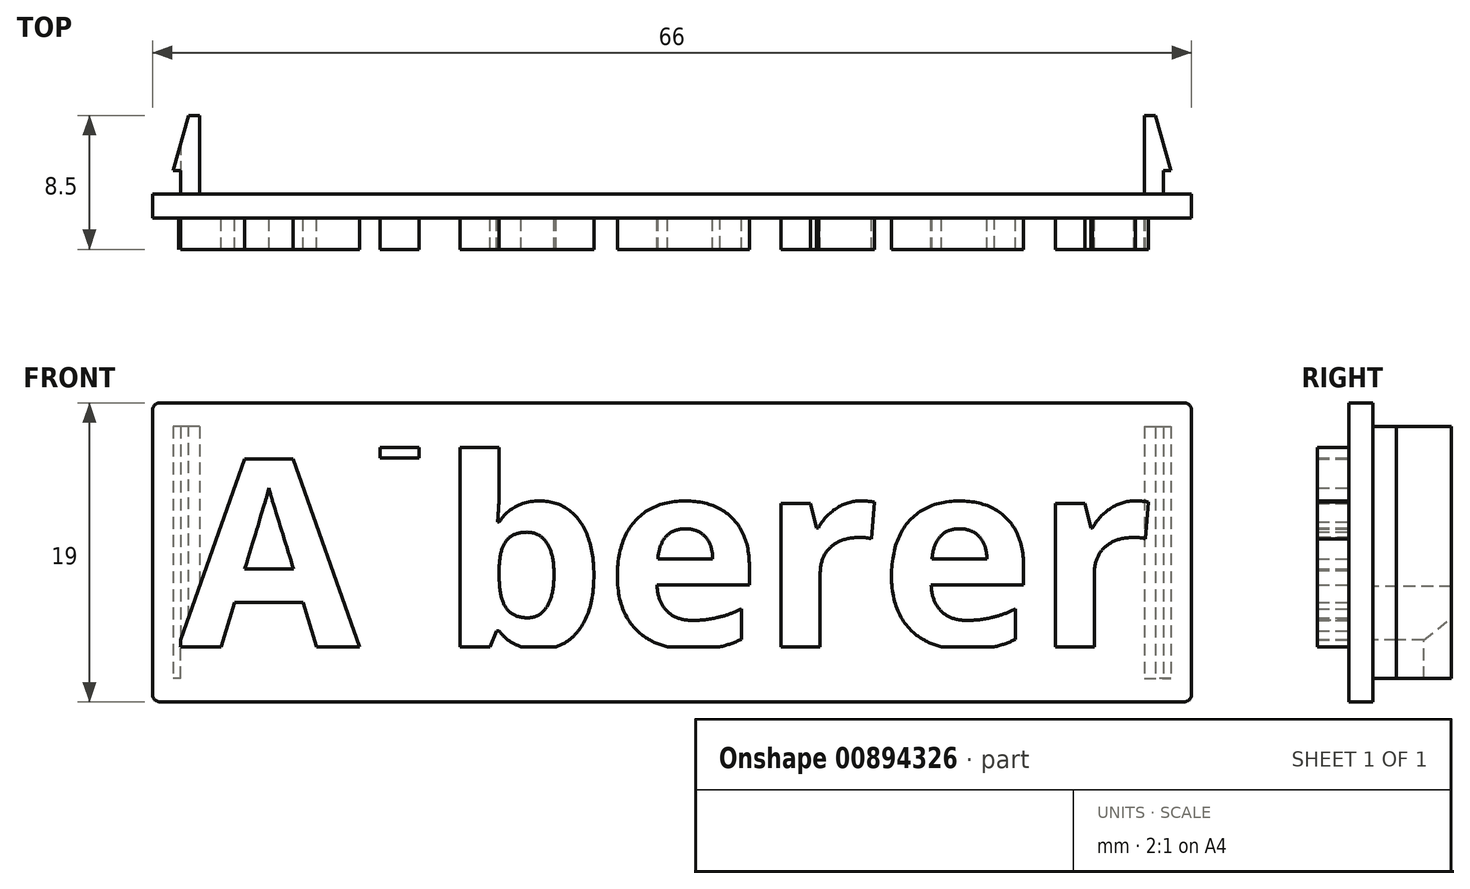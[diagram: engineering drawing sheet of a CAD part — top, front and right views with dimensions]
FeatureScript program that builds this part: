
annotation { "Feature Type Name" : "Feature", "Feature Type Description" : "" }
export const myFeature = defineFeature(function(context is Context, id is Id, definition is map)
    precondition{}
    {
        {
            var Q0;
            Q0=qCreatedBy(makeId("Front.planeOp"),FACE);
            var sketch = newSketch(context, id + "F0", { "sketchPlane" : qUnion([Q0])});
            skLineSegment(sketch, "E0.bottom", {"start": v(33, -9.5) * mm, "end": v(-33, -9.5) * mm});
            skLineSegment(sketch, "E0.top", {"start": v(33, 9.5) * mm, "end": v(-33, 9.5) * mm});
            skLineSegment(sketch, "E0.left", {"start": v(33, -9.5) * mm, "end": v(33, 9.5) * mm});
            skLineSegment(sketch, "E0.right", {"start": v(-33, -9.5) * mm, "end": v(-33, 9.5) * mm});
            skPoint(sketch, "E0.middle", {"position": v(0, 0) * mm});
            skLineSegment(sketch, "E1.bottom", {"start": v(31.35, -6) * mm, "end": v(-31.35, -6) * mm});
            skLineSegment(sketch, "E1.top", {"start": v(31.35, 6) * mm, "end": v(-31.35, 6) * mm});
            skLineSegment(sketch, "E1.left", {"start": v(31.35, -6) * mm, "end": v(31.35, 6) * mm});
            skLineSegment(sketch, "E1.right", {"start": v(-31.35, -6) * mm, "end": v(-31.35, 6) * mm});
            skText(sketch, "E2", { "text": "Alberer", "fontName": "OpenSans-Bold.ttf"});
            skLineSegment(sketch, "E3", {"start": v(31.2, 9.5) * mm, "end": v(31.2, -9.5) * mm});
            skLineSegment(sketch, "E4", {"start": v(30, 9.5) * mm, "end": v(30, -9.5) * mm});
            skLineSegment(sketch, "E5", {"start": v(31.7, 9.5) * mm, "end": v(31.7, -9.5) * mm});
            skLineSegment(sketch, "E6.MirrorCS", {"start": v(-30, 9.5) * mm, "end": v(-30, -9.5) * mm});
            skLineSegment(sketch, "E7.MirrorCS", {"start": v(-31.2, 9.5) * mm, "end": v(-31.2, -9.5) * mm});
            skLineSegment(sketch, "E8.MirrorCS", {"start": v(-31.7, 9.5) * mm, "end": v(-31.7, -9.5) * mm});
            skLineSegment(sketch, "E9", {"start": v(-30, 8) * mm, "end": v(-31.7, 8) * mm});
            skLineSegment(sketch, "E10.MirrorCS", {"start": v(-30, -8) * mm, "end": v(-31.7, -8) * mm});
            skLineSegment(sketch, "E11.MirrorCS", {"start": v(30, 8) * mm, "end": v(31.7, 8) * mm});
            skLineSegment(sketch, "E12.MirrorCS", {"start": v(30, -8) * mm, "end": v(31.7, -8) * mm});
            const initialGuessF0  = {"E2": [-0.03135, -0.006, 1, 0, 0.012]};
            skSetInitialGuess(sketch, initialGuessF0);
            skSolve(sketch);
        }
        {
            var Q0;
            Q0 = qSketchRegion(id + "F0", true);
            var Q1;
            {var subQ0=sQuery(id+"F0.wireOp",EDGE,"E2.sketch_text.stroke-93");Q1=makeQuery(id+"F0.imprint","IMPRINT",FACE,{"disambiguationData":[TD([[makeQuery(id+"F0.imprint","IMPRINT",EDGE,{"derivedFrom":subQ0}),-1.0]])]});}
            var Q2;
            Q2=makeQuery(id+"F0.imprint","IMPRINT",FACE,{"disambiguationData":[TD([[makeQuery(id+"F0.imprint","IMPRINT",EDGE,{"derivedFrom":sQuery(id+"F0.wireOp",EDGE,"E2.sketch_text.stroke-16")}),-1.0]])]});
            var Q3;
            {var subQ0=sQuery(id+"F0.wireOp",EDGE,"E6.MirrorCS");var subQ1=sQuery(id+"F0.wireOp",EDGE,"E0.bottom");var subQ2=makeQuery(id+"F0.imprint","INTERSECT",VERTEX,{"derivedFrom":[subQ1,subQ0]});Q3=makeQuery(id+"F0.imprint","IMPRINT",FACE,{"disambiguationData":[TD([[makeQuery(id+"F0.imprint","IMPRINT",EDGE,{"disambiguationData":[TD([[subQ2,-1.0]])],"derivedFrom":subQ1}),-1.0]])]});}
            var Q4;
            {var subQ3=sQuery(id+"F0.wireOp",EDGE,"E3");var subQ5=sQuery(id+"F0.wireOp",EDGE,"E2.sketch_text.stroke-95");var subQ6=makeQuery(id+"F0.imprint","INTERSECT",VERTEX,{"derivedFrom":[subQ5,subQ3]});Q4=makeQuery(id+"F0.imprint","IMPRINT",FACE,{"disambiguationData":[TD([[makeQuery(id+"F0.imprint","IMPRINT",EDGE,{"disambiguationData":[TD([[subQ6,-1.0]])],"derivedFrom":subQ5}),-1.0]])]});}
            var Q5;
            Q5=makeQuery(id+"F0.imprint","IMPRINT",FACE,{"disambiguationData":[TD([[makeQuery(id+"F0.imprint","IMPRINT",EDGE,{"derivedFrom":sQuery(id+"F0.wireOp",EDGE,"E2.sketch_text.stroke-0")}),-1.0]])]});
            var Q6;
            Q6=makeQuery(id+"F0.imprint","IMPRINT",FACE,{"disambiguationData":[TD([[makeQuery(id+"F0.imprint","IMPRINT",EDGE,{"derivedFrom":sQuery(id+"F0.wireOp",EDGE,"E2.sketch_text.stroke-39")}),-1.0]])]});
            var Q7;
            {var subQ6=sQuery(id+"F0.wireOp",EDGE,"E0.right");Q7=makeQuery(id+"F0.imprint","IMPRINT",FACE,{"disambiguationData":[TD([[makeQuery(id+"F0.imprint","IMPRINT",EDGE,{"derivedFrom":subQ6}),-1.0]])]});}
            var Q8;
            {var subQ0=sQuery(id+"F0.wireOp",EDGE,"E6.MirrorCS");var subQ1=sQuery(id+"F0.wireOp",EDGE,"E1.top");var subQ2=makeQuery(id+"F0.imprint","INTERSECT",VERTEX,{"derivedFrom":[subQ1,subQ0]});Q8=makeQuery(id+"F0.imprint","IMPRINT",FACE,{"disambiguationData":[TD([[makeQuery(id+"F0.imprint","IMPRINT",EDGE,{"disambiguationData":[TD([[subQ2,-1.0]])],"derivedFrom":subQ1}),1.0]])]});}
            var Q9;
            Q9=makeQuery(id+"F0.imprint","IMPRINT",FACE,{"disambiguationData":[TD([[makeQuery(id+"F0.imprint","IMPRINT",EDGE,{"derivedFrom":sQuery(id+"F0.wireOp",EDGE,"E2.sketch_text.stroke-59")}),-1.0]])]});
            var Q10;
            {var subQ0=sQuery(id+"F0.wireOp",EDGE,"E1.right");Q10=makeQuery(id+"F0.imprint","IMPRINT",FACE,{"disambiguationData":[TD([[makeQuery(id+"F0.imprint","IMPRINT",EDGE,{"derivedFrom":subQ0}),-1.0]])]});}
            var Q11;
            {var subQ4=sQuery(id+"F0.wireOp",EDGE,"E1.left");Q11=makeQuery(id+"F0.imprint","IMPRINT",FACE,{"disambiguationData":[TD([[makeQuery(id+"F0.imprint","IMPRINT",EDGE,{"derivedFrom":subQ4}),1.0]])]});}
            var Q12;
            {var subQ3=sQuery(id+"F0.wireOp",EDGE,"E2.sketch_text.stroke-24");var subQ5=sQuery(id+"F0.wireOp",EDGE,"E1.top");var subQ7=makeQuery(id+"F0.imprint","INTERSECT",VERTEX,{"derivedFrom":[subQ5,subQ3]});Q12=makeQuery(id+"F0.imprint","IMPRINT",FACE,{"disambiguationData":[TD([[makeQuery(id+"F0.imprint","IMPRINT",EDGE,{"disambiguationData":[TD([[subQ7,-1.0]])],"derivedFrom":subQ5}),1.0]])]});}
            var Q13;
            Q13=makeQuery(id+"F0.imprint","IMPRINT",FACE,{"disambiguationData":[TD([[makeQuery(id+"F0.imprint","IMPRINT",EDGE,{"derivedFrom":sQuery(id+"F0.wireOp",EDGE,"E2.sketch_text.stroke-30")}),1.0]])]});
            var Q14;
            {var subQ4=sQuery(id+"F0.wireOp",EDGE,"E2.sketch_text.stroke-96");Q14=makeQuery(id+"F0.imprint","IMPRINT",FACE,{"disambiguationData":[TD([[makeQuery(id+"F0.imprint","IMPRINT",EDGE,{"derivedFrom":subQ4}),1.0]])]});}
            var Q15;
            {var subQ4=sQuery(id+"F0.wireOp",EDGE,"E0.left");Q15=makeQuery(id+"F0.imprint","IMPRINT",FACE,{"disambiguationData":[TD([[makeQuery(id+"F0.imprint","IMPRINT",EDGE,{"derivedFrom":subQ4}),1.0]])]});}
            var Q16;
            {var subQ0=sQuery(id+"F0.wireOp",EDGE,"E6.MirrorCS");var subQ1=sQuery(id+"F0.wireOp",EDGE,"E0.top");var subQ2=makeQuery(id+"F0.imprint","INTERSECT",VERTEX,{"derivedFrom":[subQ1,subQ0]});Q16=makeQuery(id+"F0.imprint","IMPRINT",FACE,{"disambiguationData":[TD([[makeQuery(id+"F0.imprint","IMPRINT",EDGE,{"disambiguationData":[TD([[subQ2,-1.0]])],"derivedFrom":subQ1}),1.0]])]});}
            var Q17;
            {var subQ6=sQuery(id+"F0.wireOp",EDGE,"E2.sketch_text.stroke-0");Q17=makeQuery(id+"F0.imprint","IMPRINT",FACE,{"disambiguationData":[TD([[makeQuery(id+"F0.imprint","IMPRINT",EDGE,{"derivedFrom":subQ6}),1.0]])]});}
            var Q18;
            {var subQ3=sQuery(id+"F0.wireOp",EDGE,"E2.sketch_text.stroke-4");var subQ5=sQuery(id+"F0.wireOp",EDGE,"E7.MirrorCS");var subQ6=makeQuery(id+"F0.imprint","INTERSECT",VERTEX,{"derivedFrom":[subQ3,subQ5]});Q18=makeQuery(id+"F0.imprint","IMPRINT",FACE,{"disambiguationData":[TD([[makeQuery(id+"F0.imprint","IMPRINT",EDGE,{"disambiguationData":[TD([[subQ6,-1.0]])],"derivedFrom":subQ3}),-1.0]])]});}
            var Q19;
            {var subQ1=sQuery(id+"F0.wireOp",EDGE,"E2.sketch_text.stroke-3");var subQ3=sQuery(id+"F0.wireOp",EDGE,"E8.MirrorCS");var subQ4=makeQuery(id+"F0.imprint","INTERSECT",VERTEX,{"derivedFrom":[subQ1,subQ3]});Q19=makeQuery(id+"F0.imprint","IMPRINT",FACE,{"disambiguationData":[TD([[makeQuery(id+"F0.imprint","IMPRINT",EDGE,{"disambiguationData":[TD([[subQ4,1.0]])],"derivedFrom":subQ3}),-1.0]])]});}
            var Q20;
            {var subQ0=sQuery(id+"F0.wireOp",EDGE,"E3");var subQ1=sQuery(id+"F0.wireOp",EDGE,"E1.top");var subQ2=makeQuery(id+"F0.imprint","INTERSECT",VERTEX,{"derivedFrom":[subQ1,subQ0]});Q20=makeQuery(id+"F0.imprint","IMPRINT",FACE,{"disambiguationData":[TD([[makeQuery(id+"F0.imprint","IMPRINT",EDGE,{"disambiguationData":[TD([[subQ2,-1.0]])],"derivedFrom":subQ1}),1.0]])]});}
            var Q21;
            {var subQ1=sQuery(id+"F0.wireOp",EDGE,"E2.sketch_text.stroke-7");Q21=makeQuery(id+"F0.imprint","IMPRINT",FACE,{"disambiguationData":[TD([[makeQuery(id+"F0.imprint","IMPRINT",EDGE,{"derivedFrom":subQ1}),1.0]])]});}
            var Q22;
            Q22=makeQuery(id+"F0.imprint","IMPRINT",FACE,{"disambiguationData":[TD([[makeQuery(id+"F0.imprint","IMPRINT",EDGE,{"derivedFrom":sQuery(id+"F0.wireOp",EDGE,"E2.sketch_text.stroke-72")}),1.0]])]});
            var Q23;
            {var subQ0=sQuery(id+"F0.wireOp",EDGE,"E3");var subQ1=sQuery(id+"F0.wireOp",EDGE,"E0.top");var subQ2=makeQuery(id+"F0.imprint","INTERSECT",VERTEX,{"derivedFrom":[subQ1,subQ0]});Q23=makeQuery(id+"F0.imprint","IMPRINT",FACE,{"disambiguationData":[TD([[makeQuery(id+"F0.imprint","IMPRINT",EDGE,{"disambiguationData":[TD([[subQ2,-1.0]])],"derivedFrom":subQ1}),1.0]])]});}
            var Q24;
            {var subQ0=sQuery(id+"F0.wireOp",EDGE,"E3");var subQ1=sQuery(id+"F0.wireOp",EDGE,"E1.bottom");var subQ2=makeQuery(id+"F0.imprint","INTERSECT",VERTEX,{"derivedFrom":[subQ1,subQ0]});Q24=makeQuery(id+"F0.imprint","IMPRINT",FACE,{"disambiguationData":[TD([[makeQuery(id+"F0.imprint","IMPRINT",EDGE,{"disambiguationData":[TD([[subQ2,-1.0]])],"derivedFrom":subQ1}),-1.0]])]});}
            var Q25;
            {var subQ0=sQuery(id+"F0.wireOp",EDGE,"E3");var subQ1=sQuery(id+"F0.wireOp",EDGE,"E0.bottom");var subQ2=makeQuery(id+"F0.imprint","INTERSECT",VERTEX,{"derivedFrom":[subQ1,subQ0]});Q25=makeQuery(id+"F0.imprint","IMPRINT",FACE,{"disambiguationData":[TD([[makeQuery(id+"F0.imprint","IMPRINT",EDGE,{"disambiguationData":[TD([[subQ2,-1.0]])],"derivedFrom":subQ1}),-1.0]])]});}
            var Q26;
            {var subQ5=sQuery(id+"F0.wireOp",EDGE,"E2.sketch_text.stroke-12");Q26=makeQuery(id+"F0.imprint","IMPRINT",FACE,{"disambiguationData":[TD([[makeQuery(id+"F0.imprint","IMPRINT",EDGE,{"derivedFrom":subQ5}),-1.0]])]});}
            var Q27;
            {var subQ7=sQuery(id+"F0.wireOp",EDGE,"E2.sketch_text.stroke-14");Q27=makeQuery(id+"F0.imprint","IMPRINT",FACE,{"disambiguationData":[TD([[makeQuery(id+"F0.imprint","IMPRINT",EDGE,{"derivedFrom":subQ7}),1.0]])]});}
            var Q28;
            {var subQ0=sQuery(id+"F0.wireOp",EDGE,"E2.sketch_text.stroke-5");Q28=makeQuery(id+"F0.imprint","IMPRINT",FACE,{"disambiguationData":[TD([[makeQuery(id+"F0.imprint","IMPRINT",EDGE,{"derivedFrom":subQ0}),1.0]])]});}
            var Q29;
            Q29=makeQuery(id+"F0.imprint","IMPRINT",FACE,{"disambiguationData":[TD([[makeQuery(id+"F0.imprint","IMPRINT",EDGE,{"derivedFrom":sQuery(id+"F0.wireOp",EDGE,"E2.sketch_text.stroke-16")}),1.0]])]});
            var Q30;
            Q30=makeQuery(id+"F0.imprint","IMPRINT",FACE,{"disambiguationData":[TD([[makeQuery(id+"F0.imprint","IMPRINT",EDGE,{"derivedFrom":sQuery(id+"F0.wireOp",EDGE,"E2.sketch_text.stroke-8")}),1.0]])]});
            var Q31;
            {var subQ0=sQuery(id+"F0.wireOp",EDGE,"E2.sketch_text.stroke-96");Q31=makeQuery(id+"F0.imprint","IMPRINT",FACE,{"disambiguationData":[TD([[makeQuery(id+"F0.imprint","IMPRINT",EDGE,{"derivedFrom":subQ0}),-1.0]])]});}
            var Q32;
            {var subQ1=sQuery(id+"F0.wireOp",EDGE,"E1.bottom");var subQ3=sQuery(id+"F0.wireOp",EDGE,"E6.MirrorCS");var subQ4=makeQuery(id+"F0.imprint","INTERSECT",VERTEX,{"derivedFrom":[subQ1,subQ3]});Q32=makeQuery(id+"F0.imprint","IMPRINT",FACE,{"disambiguationData":[TD([[makeQuery(id+"F0.imprint","IMPRINT",EDGE,{"disambiguationData":[TD([[subQ4,1.0]])],"derivedFrom":subQ3}),-1.0]])]});}
            var Q33;
            Q33=makeQuery(id+"F0.imprint","IMPRINT",FACE,{"disambiguationData":[TD([[makeQuery(id+"F0.imprint","IMPRINT",EDGE,{"derivedFrom":sQuery(id+"F0.wireOp",EDGE,"E2.sketch_text.stroke-72")}),-1.0]])]});
            var Q34;
            {var subQ4=sQuery(id+"F0.wireOp",EDGE,"E2.sketch_text.stroke-21");Q34=makeQuery(id+"F0.imprint","IMPRINT",FACE,{"disambiguationData":[TD([[makeQuery(id+"F0.imprint","IMPRINT",EDGE,{"derivedFrom":subQ4}),1.0]])]});}
            var Q35;
            Q35=makeQuery(id+"F0.imprint","IMPRINT",FACE,{"disambiguationData":[TD([[makeQuery(id+"F0.imprint","IMPRINT",EDGE,{"derivedFrom":sQuery(id+"F0.wireOp",EDGE,"E2.sketch_text.stroke-39")}),1.0]])]});
            var Q36;
            {var subQ0=sQuery(id+"F0.wireOp",EDGE,"E7.MirrorCS");var subQ1=sQuery(id+"F0.wireOp",EDGE,"E0.top");var subQ2=makeQuery(id+"F0.imprint","INTERSECT",VERTEX,{"derivedFrom":[subQ1,subQ0]});Q36=makeQuery(id+"F0.imprint","IMPRINT",FACE,{"disambiguationData":[TD([[makeQuery(id+"F0.imprint","IMPRINT",EDGE,{"disambiguationData":[TD([[subQ2,-1.0]])],"derivedFrom":subQ1}),1.0]])]});}
            var Q37;
            {var subQ0=sQuery(id+"F0.wireOp",EDGE,"E2.sketch_text.stroke-104");var subQ1=sQuery(id+"F0.wireOp",EDGE,"E2.sketch_text.stroke-92");var subQ2=makeQuery(id+"F0.imprint","INTERSECT",VERTEX,{"derivedFrom":[subQ1,subQ0]});Q37=makeQuery(id+"F0.imprint","IMPRINT",FACE,{"disambiguationData":[TD([[makeQuery(id+"F0.imprint","IMPRINT",EDGE,{"disambiguationData":[TD([[subQ2,-1.0]])],"derivedFrom":subQ1}),-1.0]])]});}
            var Q38;
            {var subQ5=sQuery(id+"F0.wireOp",EDGE,"E1.top");var subQ7=sQuery(id+"F0.wireOp",EDGE,"E5");var subQ9=makeQuery(id+"F0.imprint","INTERSECT",VERTEX,{"derivedFrom":[subQ5,subQ7]});Q38=makeQuery(id+"F0.imprint","IMPRINT",FACE,{"disambiguationData":[TD([[makeQuery(id+"F0.imprint","IMPRINT",EDGE,{"disambiguationData":[TD([[subQ9,-1.0]])],"derivedFrom":subQ5}),1.0]])]});}
            var Q39;
            {var subQ0=sQuery(id+"F0.wireOp",EDGE,"E7.MirrorCS");var subQ1=sQuery(id+"F0.wireOp",EDGE,"E1.top");var subQ2=makeQuery(id+"F0.imprint","INTERSECT",VERTEX,{"derivedFrom":[subQ1,subQ0]});Q39=makeQuery(id+"F0.imprint","IMPRINT",FACE,{"disambiguationData":[TD([[makeQuery(id+"F0.imprint","IMPRINT",EDGE,{"disambiguationData":[TD([[subQ2,-1.0]])],"derivedFrom":subQ1}),1.0]])]});}
            var Q40;
            {var subQ5=sQuery(id+"F0.wireOp",EDGE,"E2.sketch_text.stroke-14");Q40=makeQuery(id+"F0.imprint","IMPRINT",FACE,{"disambiguationData":[TD([[makeQuery(id+"F0.imprint","IMPRINT",EDGE,{"derivedFrom":subQ5}),-1.0]])]});}
            var Q41;
            {var subQ1=sQuery(id+"F0.wireOp",EDGE,"E1.bottom");var subQ7=sQuery(id+"F0.wireOp",EDGE,"E5");var subQ9=makeQuery(id+"F0.imprint","INTERSECT",VERTEX,{"derivedFrom":[subQ1,subQ7]});Q41=makeQuery(id+"F0.imprint","IMPRINT",FACE,{"disambiguationData":[TD([[makeQuery(id+"F0.imprint","IMPRINT",EDGE,{"disambiguationData":[TD([[subQ9,-1.0]])],"derivedFrom":subQ1}),-1.0]])]});}
            var Q42;
            {var subQ0=sQuery(id+"F0.wireOp",EDGE,"E3");var subQ1=sQuery(id+"F0.wireOp",EDGE,"E0.bottom");var subQ2=makeQuery(id+"F0.imprint","INTERSECT",VERTEX,{"derivedFrom":[subQ1,subQ0]});Q42=makeQuery(id+"F0.imprint","IMPRINT",FACE,{"disambiguationData":[TD([[makeQuery(id+"F0.imprint","IMPRINT",EDGE,{"disambiguationData":[TD([[subQ2,1.0]])],"derivedFrom":subQ1}),-1.0]])]});}
            var Q43;
            {var subQ0=sQuery(id+"F0.wireOp",EDGE,"E7.MirrorCS");var subQ1=sQuery(id+"F0.wireOp",EDGE,"E0.bottom");var subQ2=makeQuery(id+"F0.imprint","INTERSECT",VERTEX,{"derivedFrom":[subQ1,subQ0]});Q43=makeQuery(id+"F0.imprint","IMPRINT",FACE,{"disambiguationData":[TD([[makeQuery(id+"F0.imprint","IMPRINT",EDGE,{"disambiguationData":[TD([[subQ2,-1.0]])],"derivedFrom":subQ1}),-1.0]])]});}
            var Q44;
            {var subQ5=sQuery(id+"F0.wireOp",EDGE,"E2.sketch_text.stroke-25");Q44=makeQuery(id+"F0.imprint","IMPRINT",FACE,{"disambiguationData":[TD([[makeQuery(id+"F0.imprint","IMPRINT",EDGE,{"derivedFrom":subQ5}),-1.0]])]});}
            var Q45;
            {var subQ0=sQuery(id+"F0.wireOp",EDGE,"E7.MirrorCS");var subQ1=sQuery(id+"F0.wireOp",EDGE,"E2.sketch_text.stroke-3");var subQ2=makeQuery(id+"F0.imprint","INTERSECT",VERTEX,{"derivedFrom":[subQ1,subQ0]});Q45=makeQuery(id+"F0.imprint","IMPRINT",FACE,{"disambiguationData":[TD([[makeQuery(id+"F0.imprint","IMPRINT",EDGE,{"disambiguationData":[TD([[subQ2,-1.0]])],"derivedFrom":subQ1}),-1.0]])]});}
            var Q46;
            {var subQ0=sQuery(id+"F0.wireOp",EDGE,"E3");var subQ1=sQuery(id+"F0.wireOp",EDGE,"E0.top");var subQ2=makeQuery(id+"F0.imprint","INTERSECT",VERTEX,{"derivedFrom":[subQ1,subQ0]});Q46=makeQuery(id+"F0.imprint","IMPRINT",FACE,{"disambiguationData":[TD([[makeQuery(id+"F0.imprint","IMPRINT",EDGE,{"disambiguationData":[TD([[subQ2,1.0]])],"derivedFrom":subQ1}),1.0]])]});}
            var Q47;
            {var subQ5=sQuery(id+"F0.wireOp",EDGE,"E2.sketch_text.stroke-91");Q47=makeQuery(id+"F0.imprint","IMPRINT",FACE,{"disambiguationData":[TD([[makeQuery(id+"F0.imprint","IMPRINT",EDGE,{"derivedFrom":subQ5}),-1.0]])]});}
            var Q48;
            {var subQ0=sQuery(id+"F0.wireOp",EDGE,"E2.sketch_text.stroke-19");var subQ1=sQuery(id+"F0.wireOp",EDGE,"E1.bottom");var subQ2=makeQuery(id+"F0.imprint","INTERSECT",VERTEX,{"derivedFrom":[subQ1,subQ0]});Q48=makeQuery(id+"F0.imprint","IMPRINT",FACE,{"disambiguationData":[TD([[makeQuery(id+"F0.imprint","IMPRINT",EDGE,{"disambiguationData":[TD([[subQ2,-1.0]])],"derivedFrom":subQ1}),1.0]])]});}
            var Q49;
            {var subQ5=sQuery(id+"F0.wireOp",EDGE,"E2.sketch_text.stroke-58");Q49=makeQuery(id+"F0.imprint","IMPRINT",FACE,{"disambiguationData":[TD([[makeQuery(id+"F0.imprint","IMPRINT",EDGE,{"derivedFrom":subQ5}),-1.0]])]});}
            var Q50;
            {var subQ0=sQuery(id+"F0.wireOp",EDGE,"E6.MirrorCS");var subQ1=sQuery(id+"F0.wireOp",EDGE,"E1.top");var subQ2=makeQuery(id+"F0.imprint","INTERSECT",VERTEX,{"derivedFrom":[subQ1,subQ0]});Q50=makeQuery(id+"F0.imprint","IMPRINT",FACE,{"disambiguationData":[TD([[makeQuery(id+"F0.imprint","IMPRINT",EDGE,{"disambiguationData":[TD([[subQ2,-1.0]])],"derivedFrom":subQ1}),-1.0]])]});}
            var Q51;
            {var subQ0=sQuery(id+"F0.wireOp",EDGE,"E7.MirrorCS");var subQ1=sQuery(id+"F0.wireOp",EDGE,"E1.top");var subQ2=makeQuery(id+"F0.imprint","INTERSECT",VERTEX,{"derivedFrom":[subQ1,subQ0]});Q51=makeQuery(id+"F0.imprint","IMPRINT",FACE,{"disambiguationData":[TD([[makeQuery(id+"F0.imprint","IMPRINT",EDGE,{"disambiguationData":[TD([[subQ2,-1.0]])],"derivedFrom":subQ1}),-1.0]])]});}
            var Q52;
            {var subQ0=sQuery(id+"F0.wireOp",EDGE,"E7.MirrorCS");var subQ1=sQuery(id+"F0.wireOp",EDGE,"E2.sketch_text.stroke-3");var subQ2=makeQuery(id+"F0.imprint","INTERSECT",VERTEX,{"derivedFrom":[subQ1,subQ0]});Q52=makeQuery(id+"F0.imprint","IMPRINT",FACE,{"disambiguationData":[TD([[makeQuery(id+"F0.imprint","IMPRINT",EDGE,{"disambiguationData":[TD([[subQ2,-1.0]])],"derivedFrom":subQ1}),1.0]])]});}
            var Q53;
            {var subQ0=sQuery(id+"F0.wireOp",EDGE,"E10.MirrorCS");var subQ1=sQuery(id+"F0.wireOp",EDGE,"E6.MirrorCS");var subQ2=makeQuery(id+"F0.imprint","INTERSECT",VERTEX,{"derivedFrom":[subQ1,subQ0]});Q53=makeQuery(id+"F0.imprint","IMPRINT",FACE,{"disambiguationData":[TD([[makeQuery(id+"F0.imprint","IMPRINT",EDGE,{"disambiguationData":[TD([[subQ2,1.0]])],"derivedFrom":subQ1}),-1.0]])]});}
            var Q54;
            {var subQ0=sQuery(id+"F0.wireOp",EDGE,"E5");var subQ1=sQuery(id+"F0.wireOp",EDGE,"E1.top");var subQ2=makeQuery(id+"F0.imprint","INTERSECT",VERTEX,{"derivedFrom":[subQ1,subQ0]});Q54=makeQuery(id+"F0.imprint","IMPRINT",FACE,{"disambiguationData":[TD([[makeQuery(id+"F0.imprint","IMPRINT",EDGE,{"disambiguationData":[TD([[subQ2,-1.0]])],"derivedFrom":subQ1}),-1.0]])]});}
            var Q55;
            {var subQ0=sQuery(id+"F0.wireOp",EDGE,"E3");var subQ1=sQuery(id+"F0.wireOp",EDGE,"E1.top");var subQ2=makeQuery(id+"F0.imprint","INTERSECT",VERTEX,{"derivedFrom":[subQ1,subQ0]});Q55=makeQuery(id+"F0.imprint","IMPRINT",FACE,{"disambiguationData":[TD([[makeQuery(id+"F0.imprint","IMPRINT",EDGE,{"disambiguationData":[TD([[subQ2,-1.0]])],"derivedFrom":subQ1}),-1.0]])]});}
            var Q56;
            {var subQ0=sQuery(id+"F0.wireOp",EDGE,"E5");var subQ1=sQuery(id+"F0.wireOp",EDGE,"E1.bottom");var subQ2=makeQuery(id+"F0.imprint","INTERSECT",VERTEX,{"derivedFrom":[subQ1,subQ0]});Q56=makeQuery(id+"F0.imprint","IMPRINT",FACE,{"disambiguationData":[TD([[makeQuery(id+"F0.imprint","IMPRINT",EDGE,{"disambiguationData":[TD([[subQ2,-1.0]])],"derivedFrom":subQ1}),1.0]])]});}
            var Q57;
            {var subQ0=sQuery(id+"F0.wireOp",EDGE,"E3");var subQ1=sQuery(id+"F0.wireOp",EDGE,"E1.bottom");var subQ2=makeQuery(id+"F0.imprint","INTERSECT",VERTEX,{"derivedFrom":[subQ1,subQ0]});Q57=makeQuery(id+"F0.imprint","IMPRINT",FACE,{"disambiguationData":[TD([[makeQuery(id+"F0.imprint","IMPRINT",EDGE,{"disambiguationData":[TD([[subQ2,-1.0]])],"derivedFrom":subQ1}),1.0]])]});}
            var Q58;
            {var subQ5=sQuery(id+"F0.wireOp",EDGE,"E1.left");Q58=makeQuery(id+"F0.imprint","IMPRINT",FACE,{"disambiguationData":[TD([[makeQuery(id+"F0.imprint","IMPRINT",EDGE,{"derivedFrom":subQ5}),-1.0]])]});}
            extrude(context, id + "F1", {"entities" : qUnion([Q0, Q1, Q2, Q3, Q4, Q5, Q6, Q7, Q8, Q9, Q10, Q11, Q12, Q13, Q14, Q15, Q16, Q17, Q18, Q19, Q20, Q21, Q22, Q23, Q24, Q25, Q26, Q27, Q28, Q29, Q30, Q31, Q32, Q33, Q34, Q35, Q36, Q37, Q38, Q39, Q40, Q41, Q42, Q43, Q44, Q45, Q46, Q47, Q48, Q49, Q50, Q51, Q52, Q53, Q54, Q55, Q56, Q57, Q58]), "depth" : 1.5 * mm, "offsetDistance" : 25 * mm});
        }
        {
            var Q0;
            {var subQ0=sQuery(id+"F0.wireOp",EDGE,"E2.sketch_text.stroke-96");Q0=makeQuery(id+"F0.imprint","IMPRINT",FACE,{"disambiguationData":[TD([[makeQuery(id+"F0.imprint","IMPRINT",EDGE,{"derivedFrom":subQ0}),-1.0]])]});}
            var Q1;
            {var subQ3=sQuery(id+"F0.wireOp",EDGE,"E3");var subQ5=sQuery(id+"F0.wireOp",EDGE,"E2.sketch_text.stroke-95");var subQ6=makeQuery(id+"F0.imprint","INTERSECT",VERTEX,{"derivedFrom":[subQ5,subQ3]});Q1=makeQuery(id+"F0.imprint","IMPRINT",FACE,{"disambiguationData":[TD([[makeQuery(id+"F0.imprint","IMPRINT",EDGE,{"disambiguationData":[TD([[subQ6,-1.0]])],"derivedFrom":subQ5}),-1.0]])]});}
            var Q2;
            {var subQ0=sQuery(id+"F0.wireOp",EDGE,"E2.sketch_text.stroke-104");var subQ1=sQuery(id+"F0.wireOp",EDGE,"E2.sketch_text.stroke-92");var subQ2=makeQuery(id+"F0.imprint","INTERSECT",VERTEX,{"derivedFrom":[subQ1,subQ0]});Q2=makeQuery(id+"F0.imprint","IMPRINT",FACE,{"disambiguationData":[TD([[makeQuery(id+"F0.imprint","IMPRINT",EDGE,{"disambiguationData":[TD([[subQ2,-1.0]])],"derivedFrom":subQ1}),-1.0]])]});}
            var Q3;
            {var subQ0=sQuery(id+"F0.wireOp",EDGE,"E2.sketch_text.stroke-93");Q3=makeQuery(id+"F0.imprint","IMPRINT",FACE,{"disambiguationData":[TD([[makeQuery(id+"F0.imprint","IMPRINT",EDGE,{"derivedFrom":subQ0}),-1.0]])]});}
            var Q4;
            Q4=makeQuery(id+"F0.imprint","IMPRINT",FACE,{"disambiguationData":[TD([[makeQuery(id+"F0.imprint","IMPRINT",EDGE,{"derivedFrom":sQuery(id+"F0.wireOp",EDGE,"E2.sketch_text.stroke-72")}),-1.0]])]});
            var Q5;
            Q5=makeQuery(id+"F0.imprint","IMPRINT",FACE,{"disambiguationData":[TD([[makeQuery(id+"F0.imprint","IMPRINT",EDGE,{"derivedFrom":sQuery(id+"F0.wireOp",EDGE,"E2.sketch_text.stroke-59")}),-1.0]])]});
            var Q6;
            Q6=makeQuery(id+"F0.imprint","IMPRINT",FACE,{"disambiguationData":[TD([[makeQuery(id+"F0.imprint","IMPRINT",EDGE,{"derivedFrom":sQuery(id+"F0.wireOp",EDGE,"E2.sketch_text.stroke-39")}),-1.0]])]});
            var Q7;
            Q7=makeQuery(id+"F0.imprint","IMPRINT",FACE,{"disambiguationData":[TD([[makeQuery(id+"F0.imprint","IMPRINT",EDGE,{"derivedFrom":sQuery(id+"F0.wireOp",EDGE,"E2.sketch_text.stroke-16")}),-1.0]])]});
            var Q8;
            {var subQ5=sQuery(id+"F0.wireOp",EDGE,"E2.sketch_text.stroke-25");Q8=makeQuery(id+"F0.imprint","IMPRINT",FACE,{"disambiguationData":[TD([[makeQuery(id+"F0.imprint","IMPRINT",EDGE,{"derivedFrom":subQ5}),-1.0]])]});}
            var Q9;
            {var subQ5=sQuery(id+"F0.wireOp",EDGE,"E2.sketch_text.stroke-14");Q9=makeQuery(id+"F0.imprint","IMPRINT",FACE,{"disambiguationData":[TD([[makeQuery(id+"F0.imprint","IMPRINT",EDGE,{"derivedFrom":subQ5}),-1.0]])]});}
            var Q10;
            {var subQ5=sQuery(id+"F0.wireOp",EDGE,"E2.sketch_text.stroke-12");Q10=makeQuery(id+"F0.imprint","IMPRINT",FACE,{"disambiguationData":[TD([[makeQuery(id+"F0.imprint","IMPRINT",EDGE,{"derivedFrom":subQ5}),-1.0]])]});}
            var Q11;
            Q11=makeQuery(id+"F0.imprint","IMPRINT",FACE,{"disambiguationData":[TD([[makeQuery(id+"F0.imprint","IMPRINT",EDGE,{"derivedFrom":sQuery(id+"F0.wireOp",EDGE,"E2.sketch_text.stroke-0")}),-1.0]])]});
            var Q12;
            {var subQ0=sQuery(id+"F0.wireOp",EDGE,"E7.MirrorCS");var subQ1=sQuery(id+"F0.wireOp",EDGE,"E2.sketch_text.stroke-3");var subQ2=makeQuery(id+"F0.imprint","INTERSECT",VERTEX,{"derivedFrom":[subQ1,subQ0]});Q12=makeQuery(id+"F0.imprint","IMPRINT",FACE,{"disambiguationData":[TD([[makeQuery(id+"F0.imprint","IMPRINT",EDGE,{"disambiguationData":[TD([[subQ2,-1.0]])],"derivedFrom":subQ1}),-1.0]])]});}
            var Q13;
            {var subQ3=sQuery(id+"F0.wireOp",EDGE,"E2.sketch_text.stroke-4");var subQ5=sQuery(id+"F0.wireOp",EDGE,"E7.MirrorCS");var subQ6=makeQuery(id+"F0.imprint","INTERSECT",VERTEX,{"derivedFrom":[subQ3,subQ5]});Q13=makeQuery(id+"F0.imprint","IMPRINT",FACE,{"disambiguationData":[TD([[makeQuery(id+"F0.imprint","IMPRINT",EDGE,{"disambiguationData":[TD([[subQ6,-1.0]])],"derivedFrom":subQ3}),-1.0]])]});}
            extrude(context, id + "F2", {"entities" : qUnion([Q0, Q1, Q2, Q3, Q4, Q5, Q6, Q7, Q8, Q9, Q10, Q11, Q12, Q13]), "operationType" : NewBodyOperationType.ADD, "depth" : 3.5 * mm, "offsetDistance" : 25 * mm});
        }
        {
            var Q0;
            {var subQ0=sQuery(id+"F0.wireOp",EDGE,"E6.MirrorCS");var subQ1=sQuery(id+"F0.wireOp",EDGE,"E1.top");var subQ2=makeQuery(id+"F0.imprint","INTERSECT",VERTEX,{"derivedFrom":[subQ1,subQ0]});Q0=makeQuery(id+"F0.imprint","IMPRINT",FACE,{"disambiguationData":[TD([[makeQuery(id+"F0.imprint","IMPRINT",EDGE,{"disambiguationData":[TD([[subQ2,-1.0]])],"derivedFrom":subQ1}),-1.0]])]});}
            var Q1;
            {var subQ10=sQuery(id+"F0.wireOp",EDGE,"E1.right");Q1=makeQuery(id+"F0.imprint","IMPRINT",FACE,{"disambiguationData":[TD([[makeQuery(id+"F0.imprint","IMPRINT",EDGE,{"derivedFrom":subQ10}),1.0]])]});}
            var Q2;
            {var subQ0=sQuery(id+"F0.wireOp",EDGE,"E1.right");Q2=makeQuery(id+"F0.imprint","IMPRINT",FACE,{"disambiguationData":[TD([[makeQuery(id+"F0.imprint","IMPRINT",EDGE,{"derivedFrom":subQ0}),-1.0]])]});}
            var Q3;
            {var subQ0=sQuery(id+"F0.wireOp",EDGE,"E6.MirrorCS");var subQ1=sQuery(id+"F0.wireOp",EDGE,"E1.top");var subQ2=makeQuery(id+"F0.imprint","INTERSECT",VERTEX,{"derivedFrom":[subQ1,subQ0]});Q3=makeQuery(id+"F0.imprint","IMPRINT",FACE,{"disambiguationData":[TD([[makeQuery(id+"F0.imprint","IMPRINT",EDGE,{"disambiguationData":[TD([[subQ2,-1.0]])],"derivedFrom":subQ1}),1.0]])]});}
            var Q4;
            {var subQ0=sQuery(id+"F0.wireOp",EDGE,"E6.MirrorCS");var subQ1=sQuery(id+"F0.wireOp",EDGE,"E2.sketch_text.stroke-3");var subQ2=makeQuery(id+"F0.imprint","INTERSECT",VERTEX,{"derivedFrom":[subQ1,subQ0]});Q4=makeQuery(id+"F0.imprint","IMPRINT",FACE,{"disambiguationData":[TD([[makeQuery(id+"F0.imprint","IMPRINT",EDGE,{"disambiguationData":[TD([[subQ2,-1.0]])],"derivedFrom":subQ1}),-1.0]])]});}
            var Q5;
            {var subQ0=sQuery(id+"F0.wireOp",EDGE,"E6.MirrorCS");var subQ1=sQuery(id+"F0.wireOp",EDGE,"E2.sketch_text.stroke-3");var subQ2=makeQuery(id+"F0.imprint","INTERSECT",VERTEX,{"derivedFrom":[subQ1,subQ0]});Q5=makeQuery(id+"F0.imprint","IMPRINT",FACE,{"disambiguationData":[TD([[makeQuery(id+"F0.imprint","IMPRINT",EDGE,{"disambiguationData":[TD([[subQ2,-1.0]])],"derivedFrom":subQ1}),1.0]])]});}
            var Q6;
            {var subQ0=sQuery(id+"F0.wireOp",EDGE,"E3");var subQ1=sQuery(id+"F0.wireOp",EDGE,"E1.top");var subQ2=makeQuery(id+"F0.imprint","INTERSECT",VERTEX,{"derivedFrom":[subQ1,subQ0]});Q6=makeQuery(id+"F0.imprint","IMPRINT",FACE,{"disambiguationData":[TD([[makeQuery(id+"F0.imprint","IMPRINT",EDGE,{"disambiguationData":[TD([[subQ2,-1.0]])],"derivedFrom":subQ1}),-1.0]])]});}
            var Q7;
            {var subQ5=sQuery(id+"F0.wireOp",EDGE,"E1.left");Q7=makeQuery(id+"F0.imprint","IMPRINT",FACE,{"disambiguationData":[TD([[makeQuery(id+"F0.imprint","IMPRINT",EDGE,{"derivedFrom":subQ5}),-1.0]])]});}
            var Q8;
            {var subQ0=sQuery(id+"F0.wireOp",EDGE,"E1.left");Q8=makeQuery(id+"F0.imprint","IMPRINT",FACE,{"disambiguationData":[TD([[makeQuery(id+"F0.imprint","IMPRINT",EDGE,{"derivedFrom":subQ0}),1.0]])]});}
            var Q9;
            {var subQ0=sQuery(id+"F0.wireOp",EDGE,"E2.sketch_text.stroke-93");Q9=makeQuery(id+"F0.imprint","IMPRINT",FACE,{"disambiguationData":[TD([[makeQuery(id+"F0.imprint","IMPRINT",EDGE,{"derivedFrom":subQ0}),1.0]])]});}
            var Q10;
            {var subQ0=sQuery(id+"F0.wireOp",EDGE,"E3");var subQ1=sQuery(id+"F0.wireOp",EDGE,"E1.bottom");var subQ2=makeQuery(id+"F0.imprint","INTERSECT",VERTEX,{"derivedFrom":[subQ1,subQ0]});Q10=makeQuery(id+"F0.imprint","IMPRINT",FACE,{"disambiguationData":[TD([[makeQuery(id+"F0.imprint","IMPRINT",EDGE,{"disambiguationData":[TD([[subQ2,-1.0]])],"derivedFrom":subQ1}),1.0]])]});}
            var Q11;
            {var subQ1=sQuery(id+"F0.wireOp",EDGE,"E2.sketch_text.stroke-3");var subQ3=sQuery(id+"F0.wireOp",EDGE,"E7.MirrorCS");var subQ4=makeQuery(id+"F0.imprint","INTERSECT",VERTEX,{"derivedFrom":[subQ1,subQ3]});Q11=makeQuery(id+"F0.imprint","IMPRINT",FACE,{"disambiguationData":[TD([[makeQuery(id+"F0.imprint","IMPRINT",EDGE,{"disambiguationData":[TD([[subQ4,1.0]])],"derivedFrom":subQ3}),-1.0]])]});}
            var Q12;
            {var subQ0=sQuery(id+"F0.wireOp",EDGE,"E2.sketch_text.stroke-93");Q12=makeQuery(id+"F0.imprint","IMPRINT",FACE,{"disambiguationData":[TD([[makeQuery(id+"F0.imprint","IMPRINT",EDGE,{"derivedFrom":subQ0}),-1.0]])]});}
            extrude(context, id + "F3", {"entities" : qUnion([Q0, Q1, Q2, Q3, Q4, Q5, Q6, Q7, Q8, Q9, Q10, Q11, Q12]), "operationType" : NewBodyOperationType.ADD, "depth" : -5 * mm, "offsetDistance" : 25 * mm});
        }
        {
            var Q0;
            {var subQ5=sQuery(id+"F0.wireOp",EDGE,"E1.left");Q0=makeQuery(id+"F0.imprint","IMPRINT",FACE,{"disambiguationData":[TD([[makeQuery(id+"F0.imprint","IMPRINT",EDGE,{"derivedFrom":subQ5}),-1.0]])]});}
            var Q1;
            {var subQ0=sQuery(id+"F0.wireOp",EDGE,"E1.left");Q1=makeQuery(id+"F0.imprint","IMPRINT",FACE,{"disambiguationData":[TD([[makeQuery(id+"F0.imprint","IMPRINT",EDGE,{"derivedFrom":subQ0}),1.0]])]});}
            var Q2;
            {var subQ10=sQuery(id+"F0.wireOp",EDGE,"E1.right");Q2=makeQuery(id+"F0.imprint","IMPRINT",FACE,{"disambiguationData":[TD([[makeQuery(id+"F0.imprint","IMPRINT",EDGE,{"derivedFrom":subQ10}),1.0]])]});}
            var Q3;
            {var subQ0=sQuery(id+"F0.wireOp",EDGE,"E1.right");Q3=makeQuery(id+"F0.imprint","IMPRINT",FACE,{"disambiguationData":[TD([[makeQuery(id+"F0.imprint","IMPRINT",EDGE,{"derivedFrom":subQ0}),-1.0]])]});}
            var Q4;
            {var subQ1=sQuery(id+"F0.wireOp",EDGE,"E2.sketch_text.stroke-3");var subQ3=sQuery(id+"F0.wireOp",EDGE,"E7.MirrorCS");var subQ4=makeQuery(id+"F0.imprint","INTERSECT",VERTEX,{"derivedFrom":[subQ1,subQ3]});Q4=makeQuery(id+"F0.imprint","IMPRINT",FACE,{"disambiguationData":[TD([[makeQuery(id+"F0.imprint","IMPRINT",EDGE,{"disambiguationData":[TD([[subQ4,1.0]])],"derivedFrom":subQ3}),-1.0]])]});}
            extrude(context, id + "F4", {"entities" : qUnion([Q0, Q1, Q2, Q3, Q4]), "operationType" : NewBodyOperationType.REMOVE, "oppositeDirection" : true, "depth" : 1.5 * mm, "offsetDistance" : 25 * mm});
        }
        {
            var Q0;
            Q0=makeQuery(id+"F3.opExtrude","CAP_EDGE",EDGE,{"disambiguationData":[OSD([sQuery(id+"F0.wireOp",EDGE,"E8.MirrorCS")])],"isStart":false});
            chamfer(context, id + "F5", {"entities" : qUnion([Q0]), "chamferType" : ChamferType.TWO_OFFSETS, "width1" : 3.5 * mm, "oppositeDirection" : false, "width2" : 1 * mm, "tangentPropagation" : true});
        }
        {
            var Q0;
            Q0=makeQuery(id+"F3.opExtrude","CAP_EDGE",EDGE,{"disambiguationData":[OSD([sQuery(id+"F0.wireOp",EDGE,"E5")])],"isStart":false});
            chamfer(context, id + "F6", {"entities" : qUnion([Q0]), "chamferType" : ChamferType.TWO_OFFSETS, "width1" : 1 * mm, "oppositeDirection" : false, "width2" : 3.5 * mm, "tangentPropagation" : true});
        }
        {
            var Q0;
            Q0=makeQuery(id+"F1.opExtrude","SWEPT_EDGE",EDGE,{"disambiguationData":[OSD([sQuery(id+"F0.wireOp",EDGE,"E0.top"),sQuery(id+"F0.wireOp",EDGE,"E0.left")])]});
            var Q1;
            Q1=makeQuery(id+"F1.opExtrude","SWEPT_EDGE",EDGE,{"disambiguationData":[OSD([sQuery(id+"F0.wireOp",EDGE,"E0.bottom"),sQuery(id+"F0.wireOp",EDGE,"E0.left")])]});
            var Q2;
            Q2=makeQuery(id+"F1.opExtrude","SWEPT_EDGE",EDGE,{"disambiguationData":[OSD([sQuery(id+"F0.wireOp",EDGE,"E0.bottom"),sQuery(id+"F0.wireOp",EDGE,"E0.right")])]});
            var Q3;
            Q3=makeQuery(id+"F1.opExtrude","SWEPT_EDGE",EDGE,{"disambiguationData":[OSD([sQuery(id+"F0.wireOp",EDGE,"E0.top"),sQuery(id+"F0.wireOp",EDGE,"E0.right")])]});
            fillet(context, id + "F7", {"entities" : qUnion([Q0, Q1, Q2, Q3]), "radius" : 0.5 * mm, "tangentPropagation" : true, "allowEdgeOverflow" : false});
        }
    });
